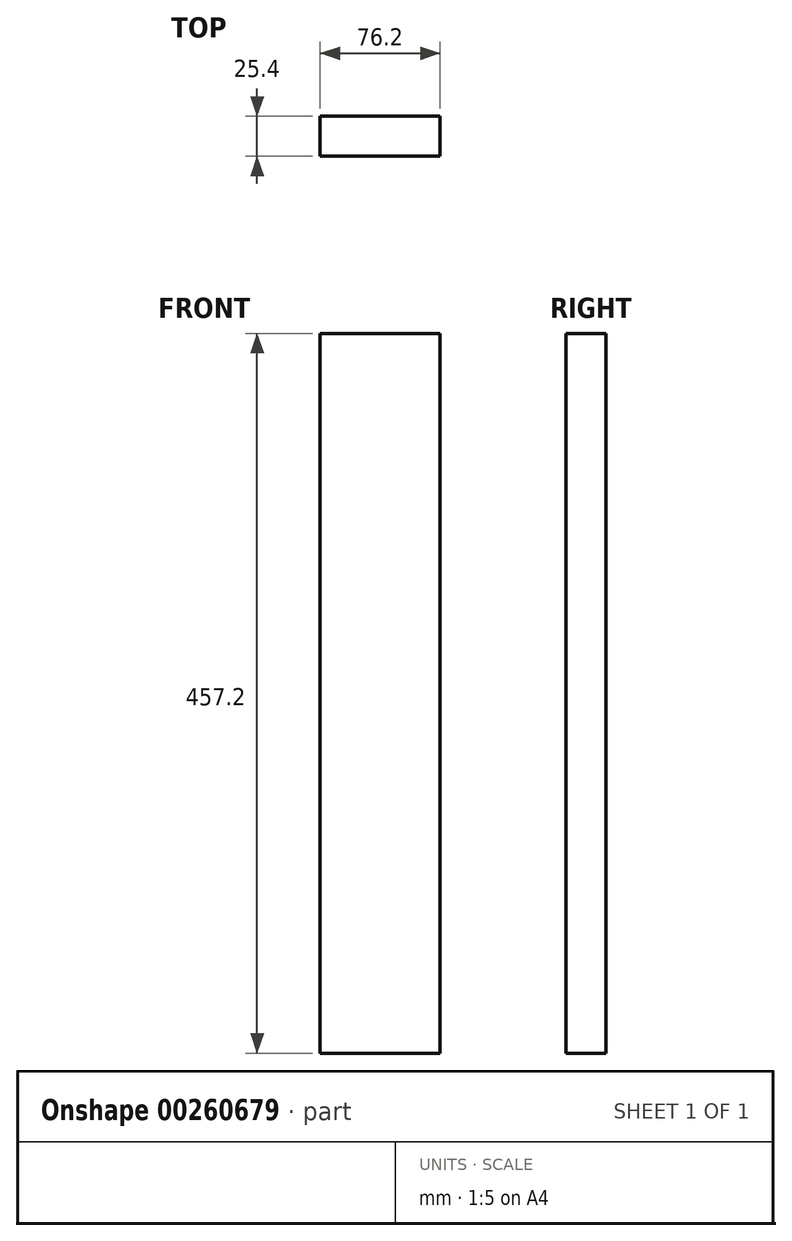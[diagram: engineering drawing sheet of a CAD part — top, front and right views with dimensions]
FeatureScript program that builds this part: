
annotation { "Feature Type Name" : "Feature", "Feature Type Description" : "" }
export const myFeature = defineFeature(function(context is Context, id is Id, definition is map)
    precondition{}
    {
        {
            var Q0;
            Q0=qCreatedBy(makeId("Top.planeOp"),FACE);
            var sketch = newSketch(context, id + "F0", { "sketchPlane" : qUnion([Q0])});
            skLineSegment(sketch, "E0", {"start": v(-39.74, 17.19) * mm, "end": v(-39.74, -8.21) * mm});
            skLineSegment(sketch, "E1", {"start": v(-39.74, -8.21) * mm, "end": v(36.46, -8.21) * mm});
            skLineSegment(sketch, "E2", {"start": v(36.46, -8.21) * mm, "end": v(36.46, 17.19) * mm});
            skLineSegment(sketch, "E3", {"start": v(36.46, 17.19) * mm, "end": v(-39.74, 17.19) * mm});
            skSolve(sketch);
        }
        {
            var Q0;
            Q0=makeQuery(id+"F0.imprint","IMPRINT",FACE,{"disambiguationData":[TD([[makeQuery(id+"F0.imprint","IMPRINT",EDGE,{"derivedFrom":sQuery(id+"F0.wireOp",EDGE,"E0")}),1.0]])]});
            extrude(context, id + "F1", {"entities" : qUnion([Q0]), "depth" : 457.2 * mm});
        }
    });
